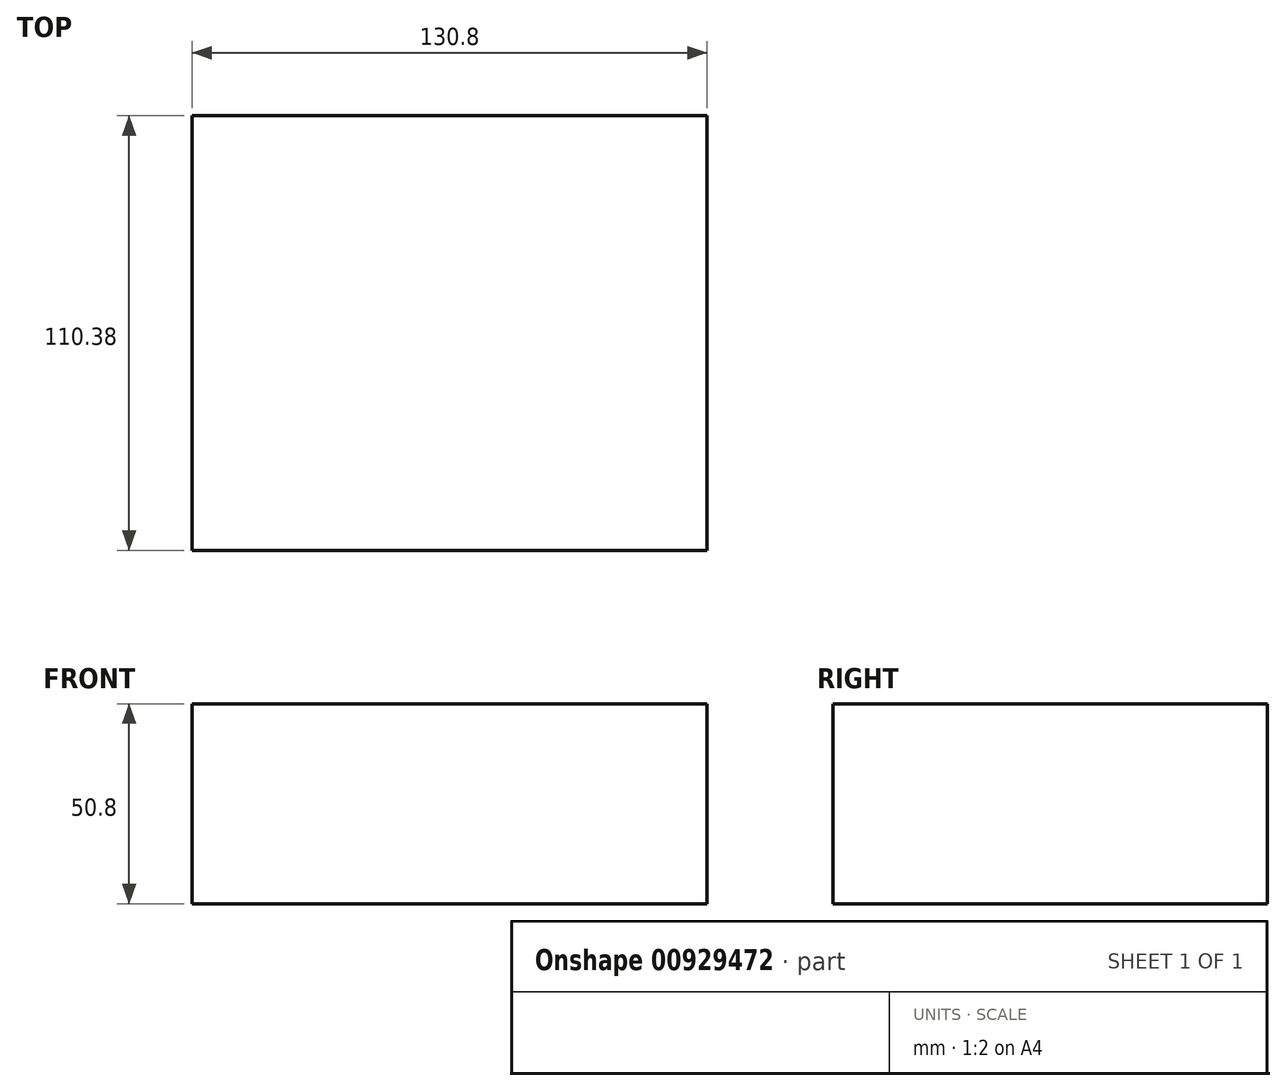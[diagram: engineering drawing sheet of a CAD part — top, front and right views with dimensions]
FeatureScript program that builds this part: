
annotation { "Feature Type Name" : "Feature", "Feature Type Description" : "" }
export const myFeature = defineFeature(function(context is Context, id is Id, definition is map)
    precondition{}
    {
        {
            var Q0;
            Q0=qCreatedBy(makeId("Top.planeOp"),FACE);
            var sketch = newSketch(context, id + "F0", { "sketchPlane" : qUnion([Q0])});
            skLineSegment(sketch, "E0.bottom", {"start": v(65.4, -55.19) * mm, "end": v(-65.4, -55.19) * mm});
            skLineSegment(sketch, "E0.top", {"start": v(65.4, 55.19) * mm, "end": v(-65.4, 55.19) * mm});
            skLineSegment(sketch, "E0.left", {"start": v(65.4, -55.19) * mm, "end": v(65.4, 55.19) * mm});
            skLineSegment(sketch, "E0.right", {"start": v(-65.4, -55.19) * mm, "end": v(-65.4, 55.19) * mm});
            skPoint(sketch, "E0.middle", {"position": v(0, 0) * mm});
            skSolve(sketch);
        }
        {
            var Q0;
            Q0 = qSketchRegion(id + "F0", true);
            extrude(context, id + "F1", {"entities" : qUnion([Q0]), "depth" : 50.8 * mm, "offsetDistance" : 25.4 * mm});
        }
    });
